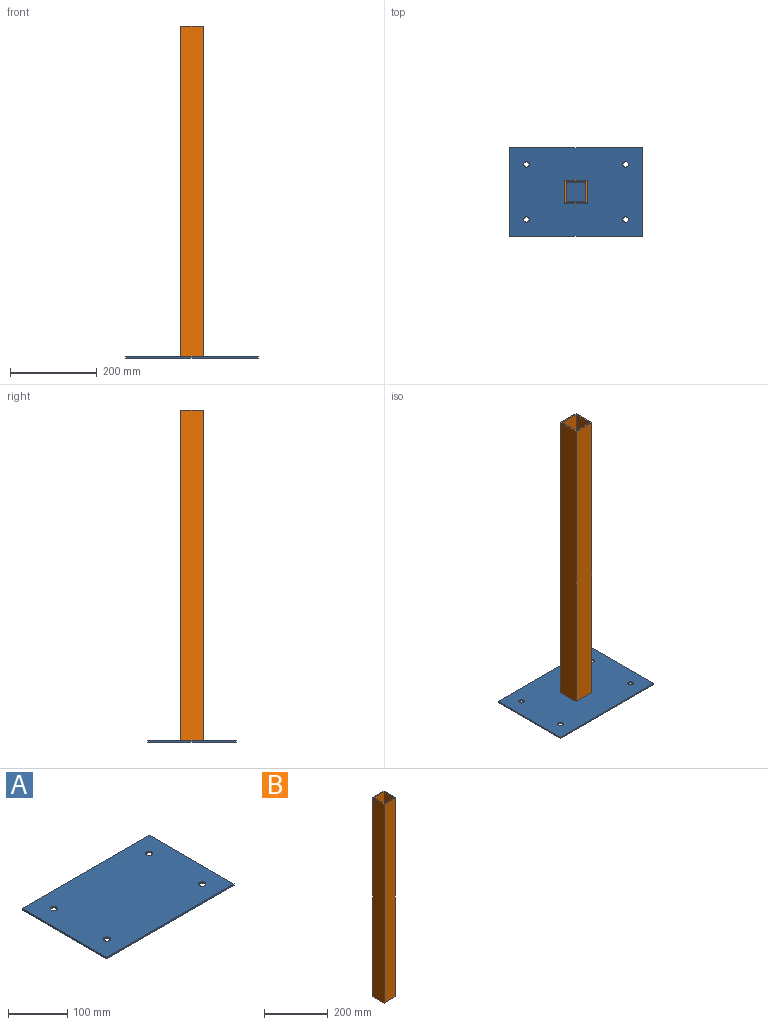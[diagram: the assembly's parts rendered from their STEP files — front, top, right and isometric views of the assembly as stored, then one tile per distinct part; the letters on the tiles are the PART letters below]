
ASSEMBLY  parts=2 mates=1
PART A: 10 faces, bbox 304.8x203.2x3.2 mm
  f0: plane 304.8x3.18mm, normal (0,1,0), area 967.7mm2, adj f1,f7,f8,f9
  f1: plane 203.2x3.18mm, normal (-1,0,0), area 645.2mm2, adj f0,f2,f8,f9
  f2: plane 304.8x3.18mm, normal (0,-1,0), area 967.7mm2, adj f1,f7,f8,f9
  f3: cylinder r=6.35mm len=12.7mm, axis (0,0,1), area 126.7mm2, adj f8,f9
  f4: cylinder r=6.35mm len=12.7mm, axis (0,0,1), area 126.7mm2, adj f8,f9
  f5: cylinder r=6.35mm len=12.7mm, axis (0,0,1), area 126.7mm2, adj f8,f9
  f6: cylinder r=6.35mm len=12.7mm, axis (0,0,1), area 126.7mm2, adj f8,f9
  f7: plane 203.2x3.18mm, normal (1,0,0), area 645.2mm2, adj f0,f2,f8,f9
  f8: plane 304.8x203.2mm, normal (0,0,-1), area 61428.7mm2, adj f0,f1,f2,f3,f4,f5,f6,f7
  f9: plane 304.8x203.2mm, normal (0,0,1), area 61428.7mm2, adj f0,f1,f2,f3,f4,f5,f6,f7
PART B: 10 faces, bbox 50.8x50.8x762 mm
  f0: plane 762x50.8mm, normal (0,1,0), area 38709.6mm2, adj f1,f7,f8,f9
  f1: plane 762x50.8mm, normal (-1,0,0), area 38709.6mm2, adj f0,f2,f8,f9
  f2: plane 762x50.8mm, normal (0,-1,0), area 38709.6mm2, adj f1,f7,f8,f9
  f3: plane 762x44.45mm, normal (1,0,0), area 33870.9mm2, adj f4,f6,f8,f9
  f4: plane 762x44.45mm, normal (0,-1,0), area 33870.9mm2, adj f3,f5,f8,f9
  f5: plane 762x44.45mm, normal (-1,0,0), area 33870.9mm2, adj f4,f6,f8,f9
  f6: plane 762x44.45mm, normal (0,1,0), area 33870.9mm2, adj f3,f5,f8,f9
  f7: plane 762x50.8mm, normal (1,0,0), area 38709.6mm2, adj f0,f2,f8,f9
  f8: plane 50.8x50.8mm, normal (0,0,1), area 604.8mm2, adj f0,f1,f2,f3,f4,f5,f6,f7
  f9: plane 50.8x50.8mm, normal (0,0,-1), area 604.8mm2, adj f0,f1,f2,f3,f4,f5,f6,f7
PLACE A at identity
PLACE B at identity
MATE fastened A.f9 <-> B.f9  axis (0,0,1) through (0,0,0)mm
